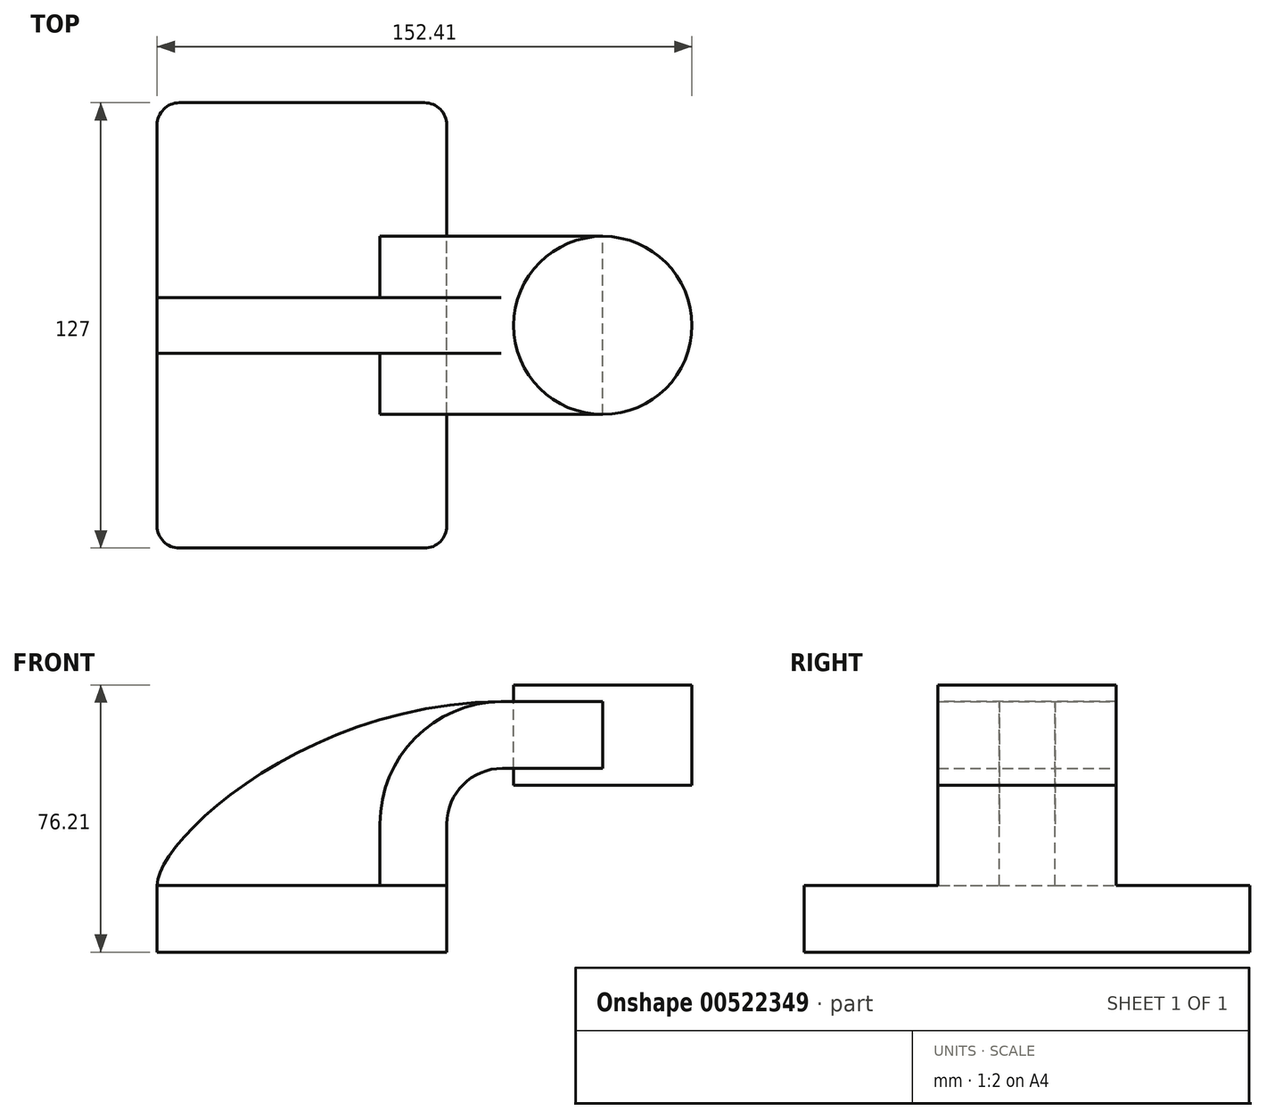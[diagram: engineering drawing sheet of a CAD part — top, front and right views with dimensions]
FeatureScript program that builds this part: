
annotation { "Feature Type Name" : "Feature", "Feature Type Description" : "" }
export const myFeature = defineFeature(function(context is Context, id is Id, definition is map)
    precondition{}
    {
        {
            var Q0;
            Q0=qCreatedBy(makeId("Front.planeOp"),FACE);
            var sketch = newSketch(context, id + "F0", { "sketchPlane" : qUnion([Q0])});
            skLineSegment(sketch, "E0.bottom", {"start": v(-41.28, -9.53) * mm, "end": v(41.28, -9.53) * mm});
            skLineSegment(sketch, "E0.top", {"start": v(-41.28, 9.52) * mm, "end": v(41.28, 9.52) * mm});
            skLineSegment(sketch, "E0.left", {"start": v(-41.28, -9.53) * mm, "end": v(-41.28, 9.52) * mm});
            skLineSegment(sketch, "E0.right", {"start": v(41.28, -9.53) * mm, "end": v(41.28, 9.52) * mm});
            skPoint(sketch, "E0.middle", {"position": v(0, 0) * mm});
            skLineSegment(sketch, "E1.bottom", {"start": v(111.12, 38.1) * mm, "end": v(60.33, 38.1) * mm});
            skLineSegment(sketch, "E1.top", {"start": v(111.12, 66.68) * mm, "end": v(60.33, 66.68) * mm});
            skLineSegment(sketch, "E1.left", {"start": v(111.12, 38.1) * mm, "end": v(111.12, 66.68) * mm});
            skLineSegment(sketch, "E1.right", {"start": v(60.33, 38.1) * mm, "end": v(60.33, 66.68) * mm});
            skPoint(sketch, "E1.middle", {"position": v(85.73, 52.39) * mm});
            skLineSegment(sketch, "E2", {"start": v(41.28, 9.52) * mm, "end": v(41.27, 27) * mm});
            skArc(sketch, "E3", {"start": v(41.27, 27) * mm, "mid": v(45.92, 38.23) * mm, "end": v(57.15, 42.88) * mm});
            skLineSegment(sketch, "E4", {"start": v(57.15, 42.88) * mm, "end": v(85.73, 42.88) * mm});
            skLineSegment(sketch, "E5.0", {"start": v(57.15, 61.93) * mm, "end": v(85.73, 61.93) * mm});
            skArc(sketch, "E5.1", {"start": v(22.22, 27) * mm, "mid": v(32.45, 51.7) * mm, "end": v(57.15, 61.93) * mm});
            skLineSegment(sketch, "E5.2", {"start": v(22.22, 9.52) * mm, "end": v(22.22, 27) * mm});
            skFitSpline(sketch, "E6", {"points": [v(-41.28, 9.52) * mm, v(57.15, 61.93) * mm], "startDerivative": vector(-1.7, 35.35) * mm, "endDerivative": vector(171.45, 0.82) * mm});
            skLineSegment(sketch, "E7", {"start": v(85.72, 66.68) * mm, "end": v(85.72, 38.1) * mm});
            skSolve(sketch);
        }
        {
            var Q0;
            Q0=makeQuery(id+"F0.imprint","IMPRINT",FACE,{"disambiguationData":[TD([[makeQuery(id+"F0.imprint","IMPRINT",EDGE,{"derivedFrom":sQuery(id+"F0.wireOp",EDGE,"E0.bottom")}),1.0]])]});
            extrude(context, id + "F1", {"entities" : qUnion([Q0]), "endBound" : BoundingType.SYMMETRIC, "depth" : 127 * mm, "offsetDistance" : 25.4 * mm});
        }
        {
            var Q0;
            {var subQ0=sQuery(id+"F0.wireOp",EDGE,"E4");var subQ1=sQuery(id+"F0.wireOp",EDGE,"E1.right");var subQ2=makeQuery(id+"F0.imprint","INTERSECT",VERTEX,{"derivedFrom":[subQ1,subQ0]});Q0=makeQuery(id+"F0.imprint","IMPRINT",FACE,{"disambiguationData":[TD([[makeQuery(id+"F0.imprint","IMPRINT",EDGE,{"disambiguationData":[TD([[subQ2,-1.0]])],"derivedFrom":subQ1}),-1.0]])]});}
            var Q1;
            {var subQ1=sQuery(id+"F0.wireOp",EDGE,"E2");Q1=makeQuery(id+"F0.imprint","IMPRINT",FACE,{"disambiguationData":[TD([[makeQuery(id+"F0.imprint","IMPRINT",EDGE,{"derivedFrom":subQ1}),1.0]])]});}
            extrude(context, id + "F2", {"entities" : qUnion([Q0, Q1]), "operationType" : NewBodyOperationType.ADD, "endBound" : BoundingType.SYMMETRIC, "depth" : 50.8 * mm, "offsetDistance" : 25.4 * mm});
        }
        {
            var Q0;
            {var subQ3=sQuery(id+"F0.wireOp",EDGE,"E5.2");Q0=makeQuery(id+"F0.imprint","IMPRINT",FACE,{"disambiguationData":[TD([[makeQuery(id+"F0.imprint","IMPRINT",EDGE,{"derivedFrom":subQ3}),1.0]])]});}
            extrude(context, id + "F3", {"entities" : qUnion([Q0]), "operationType" : NewBodyOperationType.ADD, "endBound" : BoundingType.SYMMETRIC, "depth" : 15.88 * mm, "offsetDistance" : 25.4 * mm});
        }
        {
            var Q0;
            {var subQ4=sQuery(id+"F0.wireOp",EDGE,"E1.left");Q0=makeQuery(id+"F0.imprint","IMPRINT",FACE,{"disambiguationData":[TD([[makeQuery(id+"F0.imprint","IMPRINT",EDGE,{"derivedFrom":subQ4}),1.0]])]});}
            var Q1;
            Q1=sQuery(id+"F0.wireOp",EDGE,"E7");
            revolve(context, id + "F4", {"entities" : qUnion([Q0]), "axis" : qUnion([Q1]), "revolveType" : RevolveType.FULL});
        }
        {
            var Q0;
            Q0=makeQuery(id+"F1.opExtrude","CAP_EDGE",EDGE,{"disambiguationData":[OSD([sQuery(id+"F0.wireOp",EDGE,"E0.left")])],"isStart":false});
            var Q1;
            Q1=makeQuery(id+"F1.opExtrude","CAP_EDGE",EDGE,{"disambiguationData":[OSD([sQuery(id+"F0.wireOp",EDGE,"E0.right")])],"isStart":false});
            var Q2;
            Q2=makeQuery(id+"F1.opExtrude","CAP_EDGE",EDGE,{"disambiguationData":[OSD([sQuery(id+"F0.wireOp",EDGE,"E0.right")])],"isStart":true});
            var Q3;
            Q3=makeQuery(id+"F1.opExtrude","CAP_EDGE",EDGE,{"disambiguationData":[OSD([sQuery(id+"F0.wireOp",EDGE,"E0.left")])],"isStart":true});
            fillet(context, id + "F5", {"entities" : qUnion([Q0, Q1, Q2, Q3]), "radius" : 6.35 * mm, "tangentPropagation" : true, "allowEdgeOverflow" : false});
        }
    });
